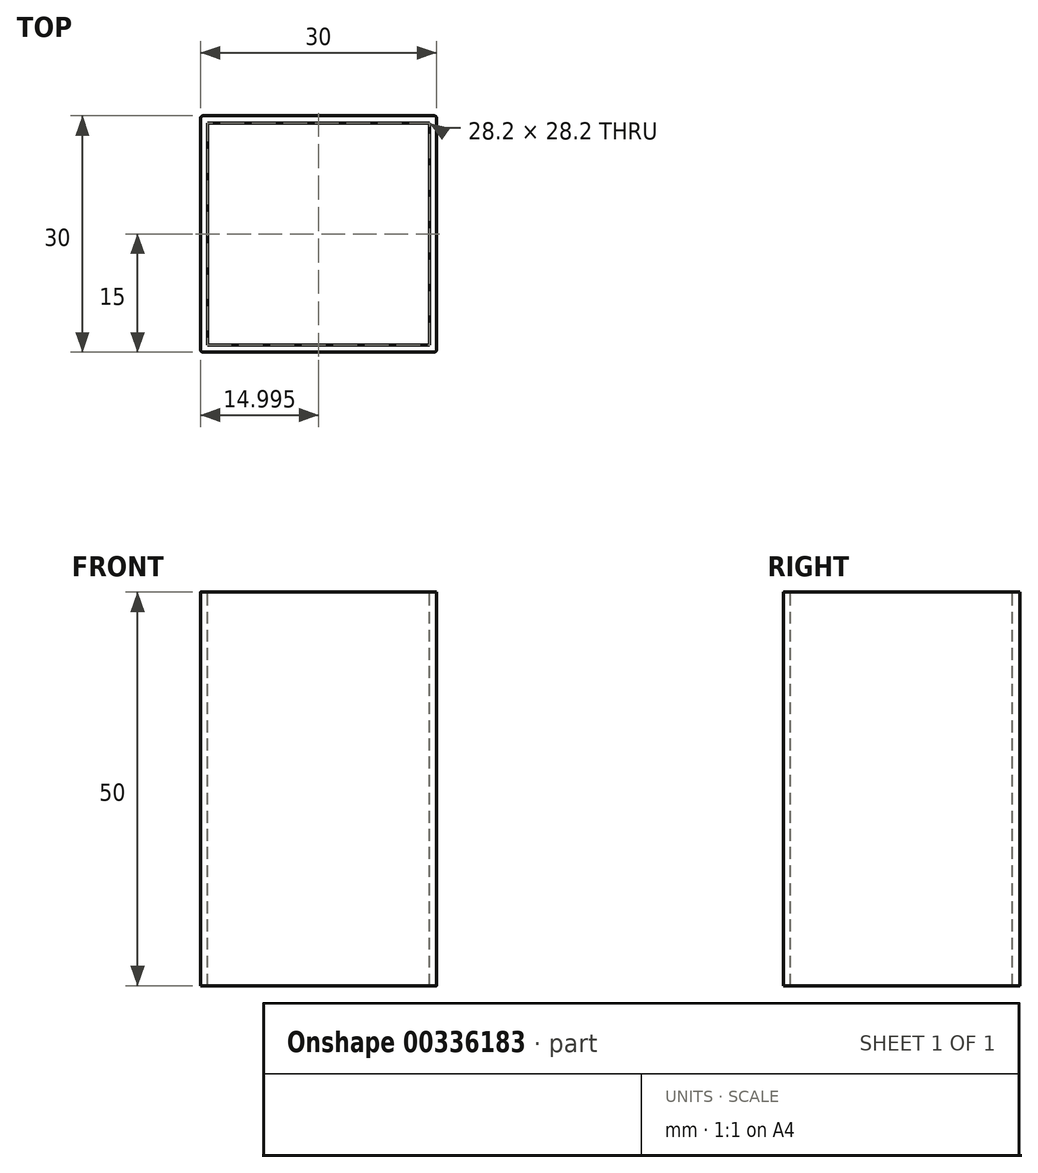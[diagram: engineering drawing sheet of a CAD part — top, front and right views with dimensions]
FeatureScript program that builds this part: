
annotation { "Feature Type Name" : "Feature", "Feature Type Description" : "" }
export const myFeature = defineFeature(function(context is Context, id is Id, definition is map)
    precondition{}
    {
        {
            var Q0;
            Q0=qCreatedBy(makeId("Front.planeOp"),FACE);
            var sketch = newSketch(context, id + "F0", { "sketchPlane" : qUnion([Q0])});
            skLineSegment(sketch, "E0.bottom", {"start": v(-14.23, 0) * mm, "end": v(15.77, 0) * mm});
            skLineSegment(sketch, "E0.top", {"start": v(-14.23, 50) * mm, "end": v(15.77, 50) * mm});
            skLineSegment(sketch, "E0.left", {"start": v(-14.23, 0) * mm, "end": v(-14.23, 50) * mm});
            skLineSegment(sketch, "E0.right", {"start": v(15.77, 0) * mm, "end": v(15.77, 50) * mm});
            skSolve(sketch);
        }
        {
            var Q0;
            Q0 = qSketchRegion(id + "F0", true);
            extrude(context, id + "F1", {"entities" : qUnion([Q0]), "depth" : 30 * mm});
        }
        {
            var Q0;
            Q0=makeQuery(id+"F1.opExtrude","SWEPT_FACE",FACE,{"disambiguationData":[OSD([sQuery(id+"F0.wireOp",EDGE,"E0.top")])]});
            var sketch = newSketch(context, id + "F2", { "sketchPlane" : qUnion([Q0])});
            skLineSegment(sketch, "E1.bottom", {"start": v(-13.33, -29.1) * mm, "end": v(14.87, -29.1) * mm});
            skLineSegment(sketch, "E1.top", {"start": v(-13.33, -0.9) * mm, "end": v(14.87, -0.9) * mm});
            skLineSegment(sketch, "E1.left", {"start": v(-13.33, -29.1) * mm, "end": v(-13.33, -0.9) * mm});
            skLineSegment(sketch, "E1.right", {"start": v(14.87, -29.1) * mm, "end": v(14.87, -0.9) * mm});
            skSolve(sketch);
        }
        {
            var Q0;
            Q0 = qSketchRegion(id + "F2", true);
            extrude(context, id + "F3", {"entities" : qUnion([Q0]), "operationType" : NewBodyOperationType.REMOVE, "endBound" : BoundingType.THROUGH_ALL, "oppositeDirection" : true, "depth" : 25 * mm});
        }
        {
            var Q0;
            Q0=makeQuery(id+"F1.opExtrude","CAP_EDGE",EDGE,{"disambiguationData":[OSD([sQuery(id+"F0.wireOp",EDGE,"E0.right")])],"isStart":false});
            var Q1;
            Q1=makeQuery(id+"F1.opExtrude","CAP_EDGE",EDGE,{"disambiguationData":[OSD([sQuery(id+"F0.wireOp",EDGE,"E0.right")])],"isStart":true});
            var Q2;
            Q2=makeQuery(id+"F1.opExtrude","CAP_EDGE",EDGE,{"disambiguationData":[OSD([sQuery(id+"F0.wireOp",EDGE,"E0.left")])],"isStart":true});
            var Q3;
            Q3=makeQuery(id+"F1.opExtrude","CAP_EDGE",EDGE,{"disambiguationData":[OSD([sQuery(id+"F0.wireOp",EDGE,"E0.left")])],"isStart":false});
            fillet(context, id + "F4", {"entities" : qUnion([Q0, Q1, Q2, Q3]), "radius" : 0.3 * mm, "tangentPropagation" : true, "allowEdgeOverflow" : false});
        }
    });
